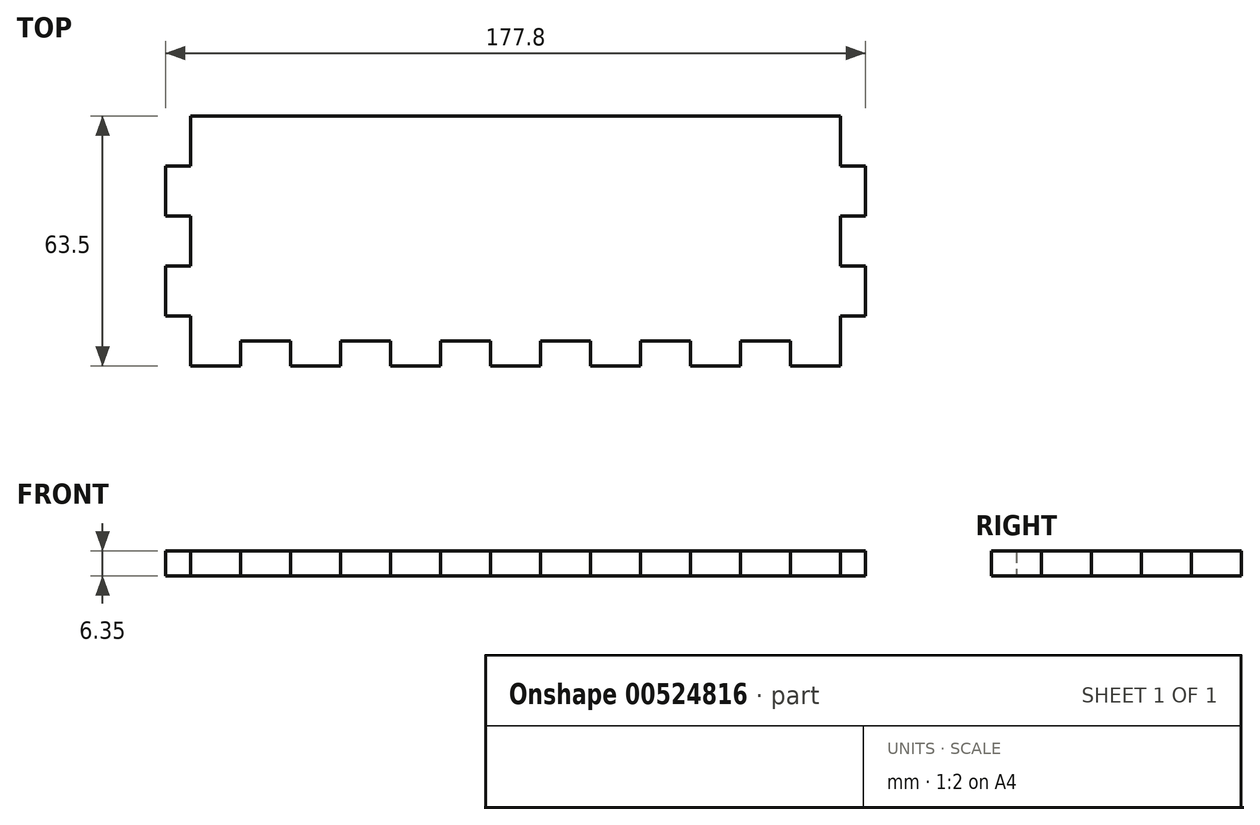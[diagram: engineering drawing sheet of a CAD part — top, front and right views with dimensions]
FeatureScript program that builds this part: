
annotation { "Feature Type Name" : "Feature", "Feature Type Description" : "" }
export const myFeature = defineFeature(function(context is Context, id is Id, definition is map)
    precondition{}
    {
        {
            var Q0;
            Q0=qCreatedBy(makeId("Top.planeOp"),FACE);
            var sketch = newSketch(context, id + "F0", { "sketchPlane" : qUnion([Q0])});
            skLineSegment(sketch, "E0.bottom", {"start": v(6.35, 0) * mm, "end": v(171.45, 0) * mm});
            skLineSegment(sketch, "E0.top", {"start": v(6.35, -63.5) * mm, "end": v(19.05, -63.5) * mm});
            skLineSegment(sketch, "E1", {"start": v(19.05, -63.5) * mm, "end": v(19.05, -57.15) * mm});
            skLineSegment(sketch, "E2", {"start": v(19.05, -57.15) * mm, "end": v(31.75, -57.15) * mm});
            skLineSegment(sketch, "E3", {"start": v(31.75, -57.15) * mm, "end": v(31.75, -63.5) * mm});
            skLineSegment(sketch, "E4", {"start": v(31.75, -63.5) * mm, "end": v(44.45, -63.5) * mm});
            skLineSegment(sketch, "E5", {"start": v(44.45, -63.5) * mm, "end": v(44.45, -57.15) * mm});
            skLineSegment(sketch, "E6", {"start": v(44.45, -57.15) * mm, "end": v(57.15, -57.15) * mm});
            skLineSegment(sketch, "E7", {"start": v(57.15, -57.15) * mm, "end": v(57.15, -63.5) * mm});
            skLineSegment(sketch, "E8", {"start": v(57.15, -63.5) * mm, "end": v(69.85, -63.5) * mm});
            skLineSegment(sketch, "E9", {"start": v(69.85, -63.5) * mm, "end": v(69.85, -57.15) * mm});
            skLineSegment(sketch, "E10", {"start": v(69.85, -57.15) * mm, "end": v(82.55, -57.15) * mm});
            skLineSegment(sketch, "E11", {"start": v(82.55, -57.15) * mm, "end": v(82.55, -63.5) * mm});
            skLineSegment(sketch, "E12.trimOffspring", {"start": v(82.55, -63.5) * mm, "end": v(95.25, -63.5) * mm});
            skLineSegment(sketch, "E13", {"start": v(95.25, -63.5) * mm, "end": v(95.25, -57.15) * mm});
            skLineSegment(sketch, "E14", {"start": v(95.25, -57.15) * mm, "end": v(107.95, -57.15) * mm});
            skLineSegment(sketch, "E15", {"start": v(107.95, -57.15) * mm, "end": v(107.95, -63.5) * mm});
            skLineSegment(sketch, "E16", {"start": v(107.95, -63.5) * mm, "end": v(120.65, -63.5) * mm});
            skLineSegment(sketch, "E17", {"start": v(120.65, -63.5) * mm, "end": v(120.65, -57.15) * mm});
            skLineSegment(sketch, "E18", {"start": v(120.65, -57.15) * mm, "end": v(133.35, -57.15) * mm});
            skLineSegment(sketch, "E19", {"start": v(133.35, -57.15) * mm, "end": v(133.35, -63.5) * mm});
            skLineSegment(sketch, "E20", {"start": v(133.35, -63.5) * mm, "end": v(146.05, -63.5) * mm});
            skLineSegment(sketch, "E21", {"start": v(146.05, -63.5) * mm, "end": v(146.05, -57.15) * mm});
            skLineSegment(sketch, "E22", {"start": v(146.05, -57.15) * mm, "end": v(158.75, -57.15) * mm});
            skLineSegment(sketch, "E23", {"start": v(158.75, -57.15) * mm, "end": v(158.75, -63.5) * mm});
            skLineSegment(sketch, "E24.trimOffspring", {"start": v(158.75, -63.5) * mm, "end": v(171.45, -63.5) * mm});
            skLineSegment(sketch, "E25", {"start": v(6.35, -63.5) * mm, "end": v(6.35, -50.8) * mm});
            skLineSegment(sketch, "E26", {"start": v(6.35, -50.8) * mm, "end": v(0, -50.8) * mm});
            skLineSegment(sketch, "E27", {"start": v(0, -50.8) * mm, "end": v(0, -38.1) * mm});
            skLineSegment(sketch, "E28", {"start": v(0, -38.1) * mm, "end": v(6.35, -38.1) * mm});
            skLineSegment(sketch, "E29", {"start": v(6.35, -38.1) * mm, "end": v(6.35, -25.4) * mm});
            skLineSegment(sketch, "E30", {"start": v(6.35, -25.4) * mm, "end": v(0, -25.4) * mm});
            skLineSegment(sketch, "E31", {"start": v(0, -25.4) * mm, "end": v(0, -12.7) * mm});
            skLineSegment(sketch, "E32", {"start": v(0, -12.7) * mm, "end": v(6.35, -12.7) * mm});
            skLineSegment(sketch, "E33", {"start": v(6.35, -12.7) * mm, "end": v(6.35, 0) * mm});
            skPoint(sketch, "E34.orphan", {"position": v(0, 0) * mm});
            skPoint(sketch, "E35.orphan", {"position": v(0, -63.5) * mm});
            skLineSegment(sketch, "E36", {"start": v(88.9, -63.5) * mm, "end": v(88.9, -41.72) * mm, "construction": true});
            skPoint(sketch, "E36.endSnap0", {"position": v(88.9, -63.5) * mm});
            skLineSegment(sketch, "E37.MirrorCS", {"start": v(171.45, -63.5) * mm, "end": v(171.45, -50.8) * mm});
            skLineSegment(sketch, "E38.MirrorCS", {"start": v(171.45, -50.8) * mm, "end": v(177.8, -50.8) * mm});
            skLineSegment(sketch, "E39.MirrorCS", {"start": v(177.8, -50.8) * mm, "end": v(177.8, -38.1) * mm});
            skLineSegment(sketch, "E40.MirrorCS", {"start": v(177.8, -38.1) * mm, "end": v(171.45, -38.1) * mm});
            skLineSegment(sketch, "E41.MirrorCS", {"start": v(171.45, -38.1) * mm, "end": v(171.45, -25.4) * mm});
            skLineSegment(sketch, "E42.MirrorCS", {"start": v(171.45, -25.4) * mm, "end": v(177.8, -25.4) * mm});
            skLineSegment(sketch, "E43.MirrorCS", {"start": v(177.8, -25.4) * mm, "end": v(177.8, -12.7) * mm});
            skLineSegment(sketch, "E44.MirrorCS", {"start": v(177.8, -12.7) * mm, "end": v(171.45, -12.7) * mm});
            skLineSegment(sketch, "E45.MirrorCS", {"start": v(171.45, -12.7) * mm, "end": v(171.45, 0) * mm});
            skPoint(sketch, "E46.orphan", {"position": v(177.8, 0) * mm});
            skSolve(sketch);
        }
        {
            var Q0;
            Q0=makeQuery(id+"F0.imprint","IMPRINT",FACE,{"disambiguationData":[TD([[makeQuery(id+"F0.imprint","IMPRINT",EDGE,{"derivedFrom":sQuery(id+"F0.wireOp",EDGE,"E0.bottom")}),-1.0]])]});
            extrude(context, id + "F1", {"entities" : qUnion([Q0]), "depth" : 6.35 * mm, "offsetDistance" : 25.4 * mm});
        }
    });
